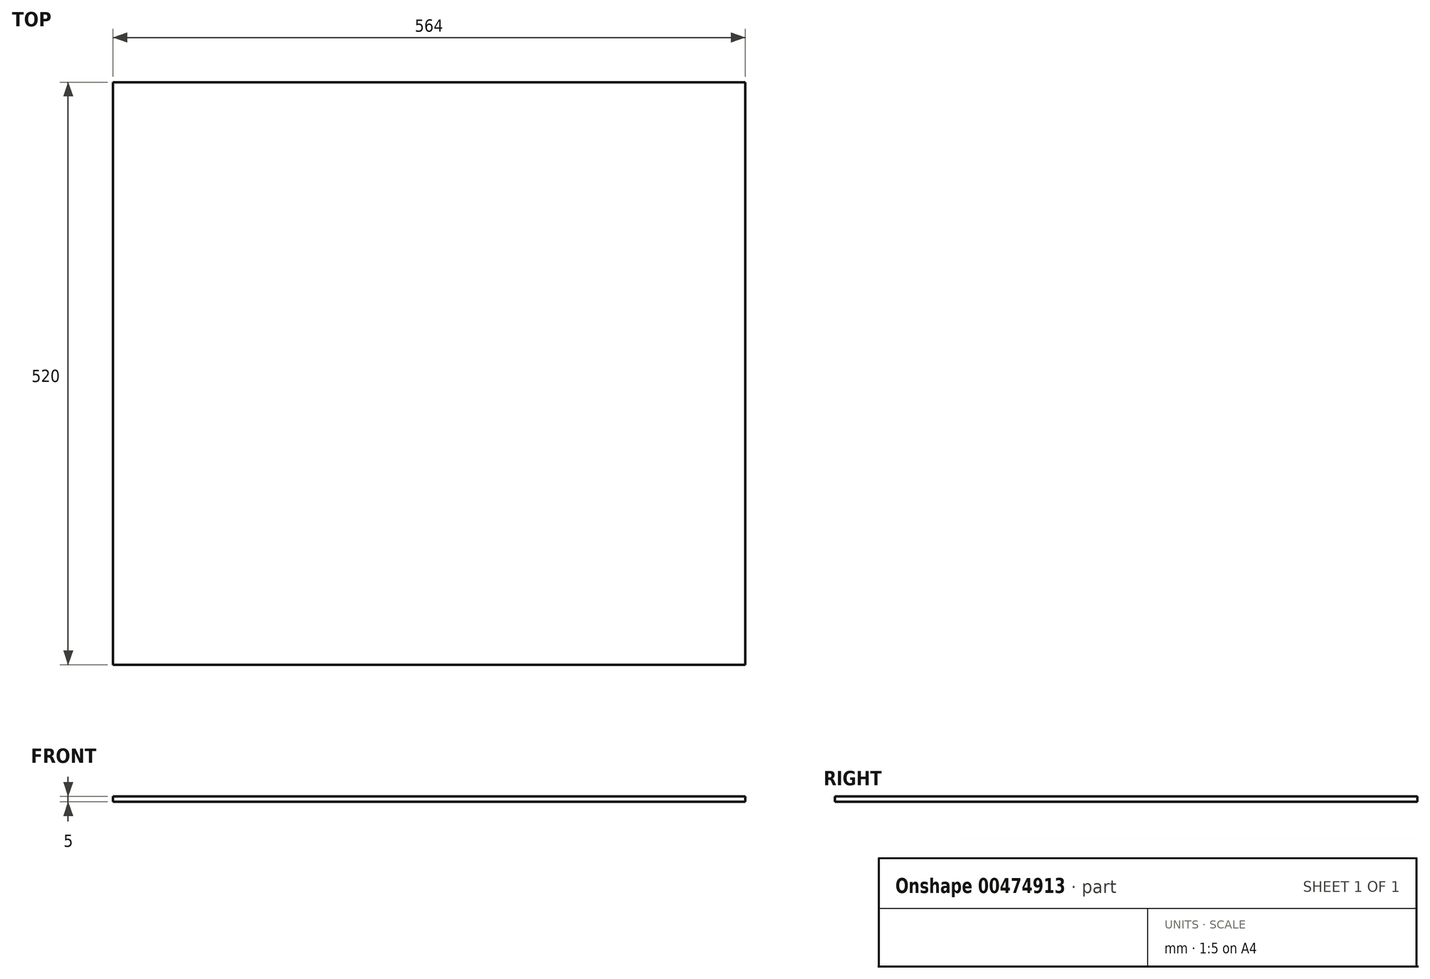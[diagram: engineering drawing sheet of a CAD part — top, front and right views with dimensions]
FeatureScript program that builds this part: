
annotation { "Feature Type Name" : "Feature", "Feature Type Description" : "" }
export const myFeature = defineFeature(function(context is Context, id is Id, definition is map)
    precondition{}
    {
        {
            var Q0;
            Q0=qCreatedBy(makeId("Top.planeOp"),FACE);
            var sketch = newSketch(context, id + "F0", { "sketchPlane" : qUnion([Q0])});
            skLineSegment(sketch, "E0.bottom", {"start": v(-336.36, 196.6) * mm, "end": v(227.64, 196.6) * mm});
            skLineSegment(sketch, "E0.top", {"start": v(-336.36, -323.4) * mm, "end": v(227.64, -323.4) * mm});
            skLineSegment(sketch, "E0.left", {"start": v(-336.36, 196.6) * mm, "end": v(-336.36, -323.4) * mm});
            skLineSegment(sketch, "E0.right", {"start": v(227.64, 196.6) * mm, "end": v(227.64, -323.4) * mm});
            skSolve(sketch);
        }
        {
            var Q0;
            Q0=makeQuery(id+"F0.imprint","IMPRINT",FACE,{"disambiguationData":[TD([[makeQuery(id+"F0.imprint","IMPRINT",EDGE,{"derivedFrom":sQuery(id+"F0.wireOp",EDGE,"E0.bottom")}),-1.0]])]});
            extrude(context, id + "F1", {"entities" : qUnion([Q0]), "depth" : 5 * mm, "offsetDistance" : 25 * mm});
        }
    });
